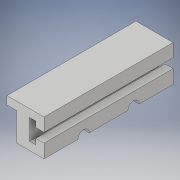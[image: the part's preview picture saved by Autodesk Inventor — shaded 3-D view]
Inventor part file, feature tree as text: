
AUTODESK INVENTOR PART (.ipt)
format: ipt  version: 2019 (Build 230136000, 136)  size: 130,560 bytes
history: native  units: mm
features: extrude x2, sketch x2, plane x1, mirror x1, projected_geometry x1
ambient origin geometry x8: Origin, YZ Plane, XZ Plane, XY Plane, X Axis, Y Axis, Z Axis, Center Point
bodies: Solid1 (feature_tree)
feature tree (7):
  extrude  "Extrusion1"  Depth=5.0mm
  extrude  "Extrusion2"  Depth=5.0mm
  plane  "Work Plane1"
  mirror  "Mirror1"
  sketch  "Sketch1"  dims[d0=6.0mm d1=5.0mm]
  sketch  "Sketch2"  dims[d4=4.0mm d8=5.0mm d10=5.8mm d12=3.5mm d13=3.5mm d15=80.0mm d16=0.0mm d17=0.3mm d18=17.0mm d19=8.0mm d20=0.0mm d21=7.0mm d22=7.0mm d24=24.5mm d25=20.0mm d26=0.0mm d27=40.0mm]
  projected_geometry  "Projected Loop1"
